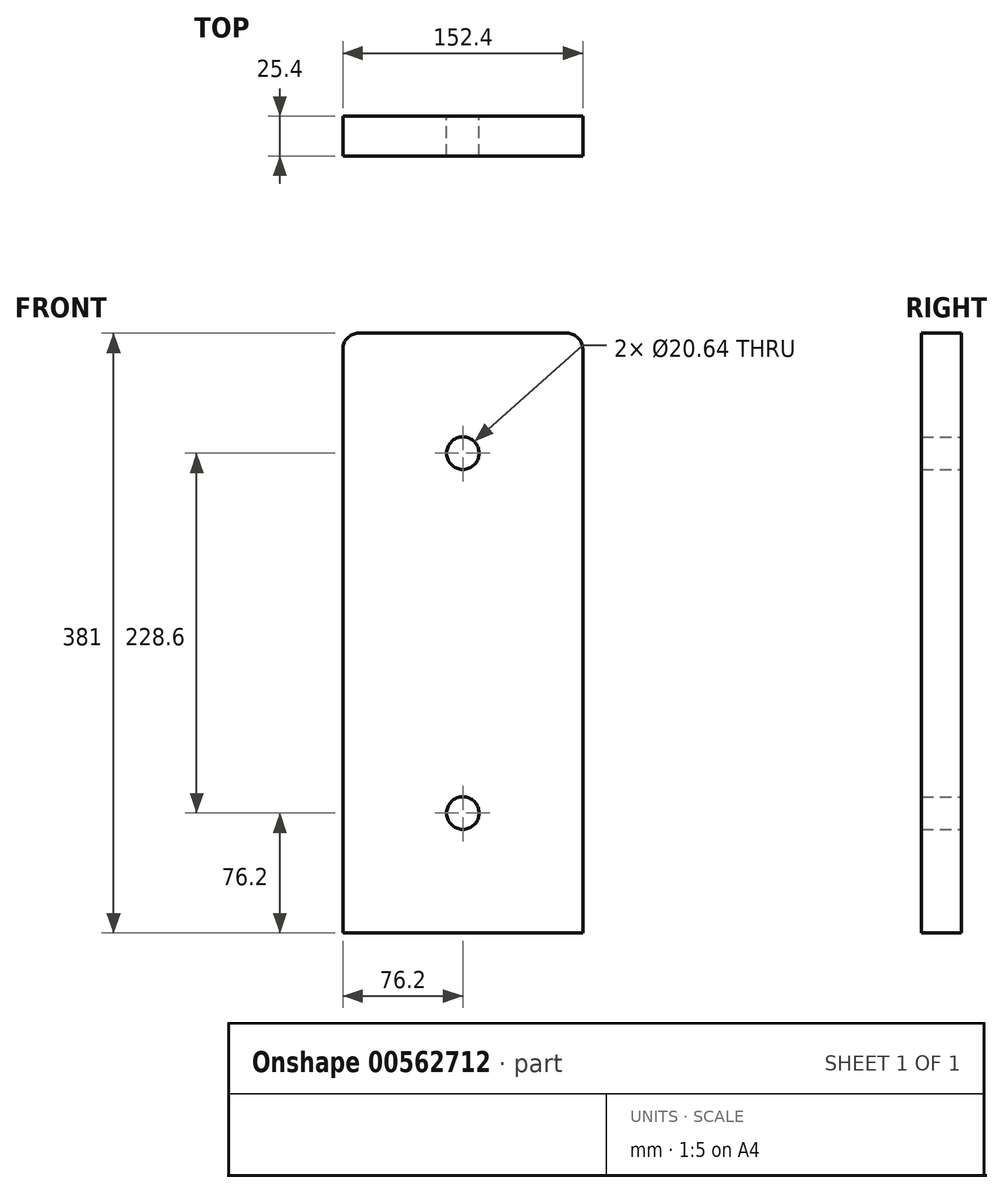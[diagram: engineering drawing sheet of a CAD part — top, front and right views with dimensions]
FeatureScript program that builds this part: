
annotation { "Feature Type Name" : "Feature", "Feature Type Description" : "" }
export const myFeature = defineFeature(function(context is Context, id is Id, definition is map)
    precondition{}
    {
        {
            var Q0;
            Q0=qCreatedBy(makeId("Front.planeOp"),FACE);
            var sketch = newSketch(context, id + "F0", { "sketchPlane" : qUnion([Q0])});
            skLineSegment(sketch, "E0.bottom", {"start": v(-76.2, 190.5) * mm, "end": v(76.2, 190.5) * mm});
            skLineSegment(sketch, "E0.top", {"start": v(-76.2, -190.5) * mm, "end": v(76.2, -190.5) * mm});
            skLineSegment(sketch, "E0.left", {"start": v(-76.2, 190.5) * mm, "end": v(-76.2, -190.5) * mm});
            skLineSegment(sketch, "E0.right", {"start": v(76.2, 190.5) * mm, "end": v(76.2, -190.5) * mm});
            skPoint(sketch, "E0.middle", {"position": v(0, 0) * mm});
            skPoint(sketch, "E1", {"position": v(0, -114.3) * mm});
            skCircle(sketch, "E2", {"center": v(0, -114.3) * mm, "radius": 10.32 * mm});
            skCircle(sketch, "E3", {"center": v(0, 114.3) * mm, "radius": 10.32 * mm});
            skSolve(sketch);
        }
        {
            var Q0;
            Q0=makeQuery(id+"F0.imprint","IMPRINT",FACE,{"disambiguationData":[TD([[makeQuery(id+"F0.imprint","IMPRINT",EDGE,{"derivedFrom":sQuery(id+"F0.wireOp",EDGE,"E0.bottom")}),-1.0]])]});
            extrude(context, id + "F1", {"entities" : qUnion([Q0]), "depth" : 25.4 * mm, "offsetDistance" : 25.4 * mm});
        }
        {
            var Q0;
            Q0=makeQuery(id+"F1.opExtrude","SWEPT_EDGE",EDGE,{"disambiguationData":[OSD([sQuery(id+"F0.wireOp",EDGE,"E0.bottom"),sQuery(id+"F0.wireOp",EDGE,"E0.left")])]});
            var Q1;
            Q1=makeQuery(id+"F1.opExtrude","SWEPT_EDGE",EDGE,{"disambiguationData":[OSD([sQuery(id+"F0.wireOp",EDGE,"E0.bottom"),sQuery(id+"F0.wireOp",EDGE,"E0.right")])]});
            fillet(context, id + "F2", {"entities" : qUnion([Q0, Q1]), "radius" : 10.16 * mm, "tangentPropagation" : true, "allowEdgeOverflow" : false});
        }
    });
